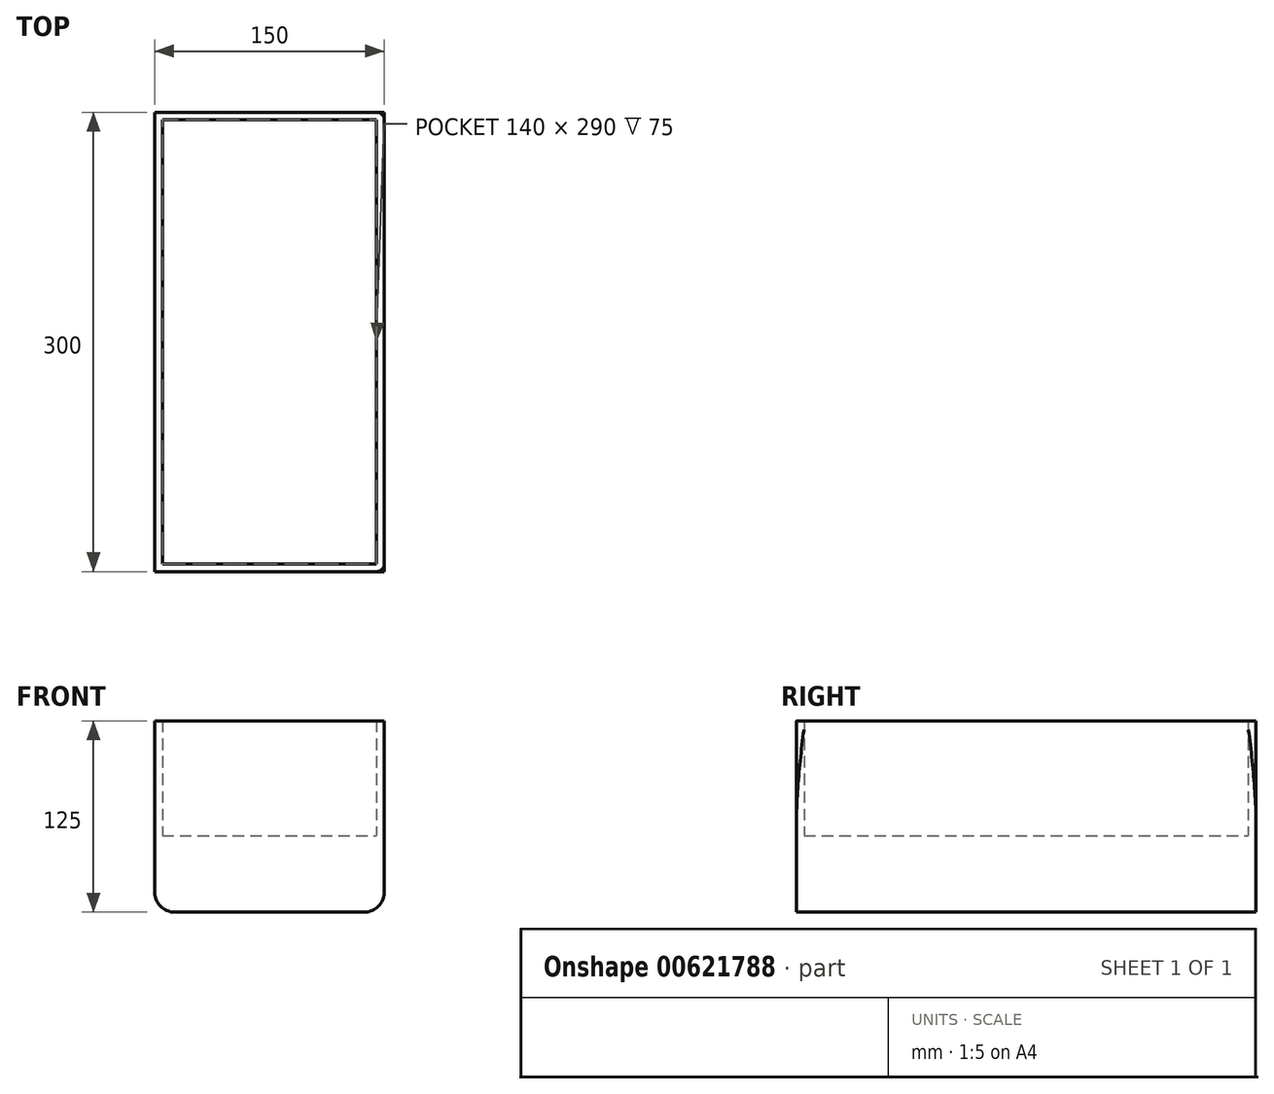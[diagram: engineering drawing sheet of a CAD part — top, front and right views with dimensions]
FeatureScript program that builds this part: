
annotation { "Feature Type Name" : "Feature", "Feature Type Description" : "" }
export const myFeature = defineFeature(function(context is Context, id is Id, definition is map)
    precondition{}
    {
        {
            var Q0;
            Q0=qCreatedBy(makeId("Front.planeOp"),FACE);
            var sketch = newSketch(context, id + "F0", { "sketchPlane" : qUnion([Q0])});
            skLineSegment(sketch, "E0", {"start": v(-74.78, 0) * mm, "end": v(-74.78, 78.48) * mm});
            skLineSegment(sketch, "E1.MirrorCS", {"start": v(-74.78, 0) * mm, "end": v(-74.78, -87) * mm});
            skLineSegment(sketch, "E2", {"start": v(-61.78, -100) * mm, "end": v(52.22, -100) * mm});
            skPoint(sketch, "E3.visualSharp", {"position": v(-74.78, 100) * mm});
            skArc(sketch, "E3.filletArc", {"start": v(-53.3, 101.43) * mm, "mid": v(-68.58, 94.2) * mm, "end": v(-74.78, 78.48) * mm});
            skPoint(sketch, "E4.visualSharp", {"position": v(-74.78, -100) * mm});
            skArc(sketch, "E4.filletArc", {"start": v(-74.78, -87) * mm, "mid": v(-70.97, -96.2) * mm, "end": v(-61.78, -100) * mm});
            skPoint(sketch, "E5.visualSharp", {"position": v(75.22, -100) * mm});
            skLineSegment(sketch, "E6", {"start": v(52.22, -100) * mm, "end": v(62.22, -100) * mm});
            skLineSegment(sketch, "E7", {"start": v(75.22, -77) * mm, "end": v(75.22, -87) * mm});
            skArc(sketch, "E8.filletArc", {"start": v(62.22, -100) * mm, "mid": v(71.41, -96.2) * mm, "end": v(75.22, -87) * mm});
            skArc(sketch, "E9", {"start": v(89, 122.82) * mm, "mid": v(78.48, 71.54) * mm, "end": v(75.22, 19.3) * mm});
            skLineSegment(sketch, "E10", {"start": v(89, 122.82) * mm, "end": v(101.58, 173.35) * mm});
            skLineSegment(sketch, "E11", {"start": v(52.3, 117.86) * mm, "end": v(77.33, 182.7) * mm});
            skArc(sketch, "E12", {"start": v(77.33, 182.7) * mm, "mid": v(94.13, 190.15) * mm, "end": v(101.58, 173.35) * mm});
            skLineSegment(sketch, "E13", {"start": v(-53.3, 101.43) * mm, "end": v(41.3, 109.59) * mm});
            skLineSegment(sketch, "E14", {"start": v(75.22, 19.3) * mm, "end": v(75.22, -77) * mm});
            skPoint(sketch, "E15.visualSharp", {"position": v(49.38, 110.29) * mm});
            skArc(sketch, "E15.filletArc", {"start": v(41.3, 109.59) * mm, "mid": v(47.98, 112.15) * mm, "end": v(52.3, 117.86) * mm});
            skLineSegment(sketch, "E16", {"start": v(-74.78, -33.86) * mm, "end": v(75.22, -33.86) * mm});
            skLineSegment(sketch, "E17", {"start": v(-74.78, -100) * mm, "end": v(-74.78, 25) * mm});
            skLineSegment(sketch, "E18", {"start": v(-74.78, 25) * mm, "end": v(75.22, 25) * mm});
            skSolve(sketch);
        }
        {
            var Q0;
            Q0=makeQuery(id+"F0.imprint","IMPRINT",FACE,{"disambiguationData":[TD([[makeQuery(id+"F0.imprint","IMPRINT",EDGE,{"derivedFrom":sQuery(id+"F0.wireOp",EDGE,"E2")}),1.0]])]});
            var Q1;
            Q1=makeQuery(id+"F0.imprint","IMPRINT",FACE,{"disambiguationData":[TD([[makeQuery(id+"F0.imprint","IMPRINT",EDGE,{"derivedFrom":sQuery(id+"F0.wireOp",EDGE,"E0")}),-1.0]])]});
            extrude(context, id + "F1", {"entities" : qUnion([Q0, Q1]), "endBound" : BoundingType.SYMMETRIC, "depth" : 300 * mm, "offsetDistance" : 25 * mm});
        }
        {
            var Q0;
            Q0=makeQuery(id+"F1.opExtrude","CAP_EDGE",EDGE,{"disambiguationData":[OSD([sQuery(id+"F0.wireOp",EDGE,"E11")])],"isStart":false});
            var Q1;
            Q1=makeQuery(id+"F1.opExtrude","CAP_EDGE",EDGE,{"disambiguationData":[OSD([sQuery(id+"F0.wireOp",EDGE,"E10")])],"isStart":false});
            var Q2;
            Q2=makeQuery(id+"F1.opExtrude","CAP_EDGE",EDGE,{"disambiguationData":[OSD([sQuery(id+"F0.wireOp",EDGE,"E12")])],"isStart":false});
            var Q3;
            Q3=makeQuery(id+"F1.opExtrude","CAP_EDGE",EDGE,{"disambiguationData":[OSD([sQuery(id+"F0.wireOp",EDGE,"E9")])],"isStart":false});
            var Q4;
            Q4=makeQuery(id+"F1.opExtrude","CAP_EDGE",EDGE,{"disambiguationData":[OSD([sQuery(id+"F0.wireOp",EDGE,"E3.filletArc")])],"isStart":false});
            var Q5;
            Q5=makeQuery(id+"F1.opExtrude","CAP_EDGE",EDGE,{"disambiguationData":[OSD([sQuery(id+"F0.wireOp",EDGE,"E17")])],"isStart":false});
            var Q6;
            Q6=makeQuery(id+"F1.opExtrude","CAP_EDGE",EDGE,{"disambiguationData":[OSD([sQuery(id+"F0.wireOp",EDGE,"E17")])],"isStart":true});
            var Q7;
            Q7=makeQuery(id+"F1.opExtrude","CAP_EDGE",EDGE,{"disambiguationData":[OSD([sQuery(id+"F0.wireOp",EDGE,"E9")])],"isStart":true});
            var Q8;
            Q8=makeQuery(id+"F1.opExtrude","CAP_EDGE",EDGE,{"disambiguationData":[OSD([sQuery(id+"F0.wireOp",EDGE,"E11")])],"isStart":true});
            var Q9;
            Q9=makeQuery(id+"F1.opExtrude","CAP_EDGE",EDGE,{"disambiguationData":[OSD([sQuery(id+"F0.wireOp",EDGE,"E10")])],"isStart":true});
            var Q10;
            Q10=makeQuery(id+"F1.opExtrude","CAP_EDGE",EDGE,{"disambiguationData":[OSD([sQuery(id+"F0.wireOp",EDGE,"E3.filletArc")])],"isStart":true});
            fillet(context, id + "F2", {"entities" : qUnion([Q0, Q1, Q2, Q3, Q4, Q5, Q6, Q7, Q8, Q9, Q10]), "radius" : 5 * mm, "tangentPropagation" : true, "allowEdgeOverflow" : false});
        }
        {
            var Q0;
            Q0=qCreatedBy(makeId("Top.planeOp"),FACE);
            var sketch = newSketch(context, id + "F3", { "sketchPlane" : qUnion([Q0])});
            skLineSegment(sketch, "E19", {"start": v(-69.78, -145) * mm, "end": v(-69.78, 145) * mm});
            skLineSegment(sketch, "E20", {"start": v(-69.78, -145) * mm, "end": v(70.22, -145) * mm});
            skLineSegment(sketch, "E21", {"start": v(70.22, 145) * mm, "end": v(70.22, -145) * mm});
            skLineSegment(sketch, "E22", {"start": v(70.22, 145) * mm, "end": v(-69.78, 145) * mm});
            skSolve(sketch);
        }
        {
            var Q0;
            Q0=makeQuery(id+"F3.imprint","IMPRINT",FACE,{"disambiguationData":[TD([[makeQuery(id+"F3.imprint","IMPRINT",EDGE,{"derivedFrom":sQuery(id+"F3.wireOp",EDGE,"E19")}),-1.0]])]});
            extrude(context, id + "F4", {"entities" : qUnion([Q0]), "endBound" : BoundingType.SYMMETRIC, "depth" : 100 * mm, "offsetDistance" : 25 * mm});
        }
        {
            var Q0;
            Q0=makeQuery(id+"F4.opExtrude","SWEPT_BODY",BODY,{"disambiguationData":[OSD([sQuery(id+"F3.wireOp",EDGE,"E19"),sQuery(id+"F3.wireOp",EDGE,"E20"),sQuery(id+"F3.wireOp",EDGE,"E21"),sQuery(id+"F3.wireOp",EDGE,"E22")])]});
            var Q1;
            Q1=makeQuery(id+"F1.opExtrude","SWEPT_BODY",BODY,{"disambiguationData":[OSD([sQuery(id+"F0.wireOp",EDGE,"E2"),sQuery(id+"F0.wireOp",EDGE,"E4.filletArc"),sQuery(id+"F0.wireOp",EDGE,"E6"),sQuery(id+"F0.wireOp",EDGE,"E7"),sQuery(id+"F0.wireOp",EDGE,"E8.filletArc"),sQuery(id+"F0.wireOp",EDGE,"E14"),sQuery(id+"F0.wireOp",EDGE,"E16"),sQuery(id+"F0.wireOp",EDGE,"E17")])]});
            var Q2;
            Q2=makeQuery(id+"F1.opExtrude","SWEPT_BODY",BODY,{"disambiguationData":[OSD([sQuery(id+"F0.wireOp",EDGE,"E0"),sQuery(id+"F0.wireOp",EDGE,"E3.filletArc"),sQuery(id+"F0.wireOp",EDGE,"E9"),sQuery(id+"F0.wireOp",EDGE,"E10"),sQuery(id+"F0.wireOp",EDGE,"E11"),sQuery(id+"F0.wireOp",EDGE,"E12"),sQuery(id+"F0.wireOp",EDGE,"E13"),sQuery(id+"F0.wireOp",EDGE,"E15.filletArc"),sQuery(id+"F0.wireOp",EDGE,"E18")])]});
            booleanBodies(context, id + "F5", {"operationType" : BooleanOperationType.SUBTRACTION, "tools" : qUnion([Q0]), "targets" : qUnion([Q1, Q2])});
        }
    });
